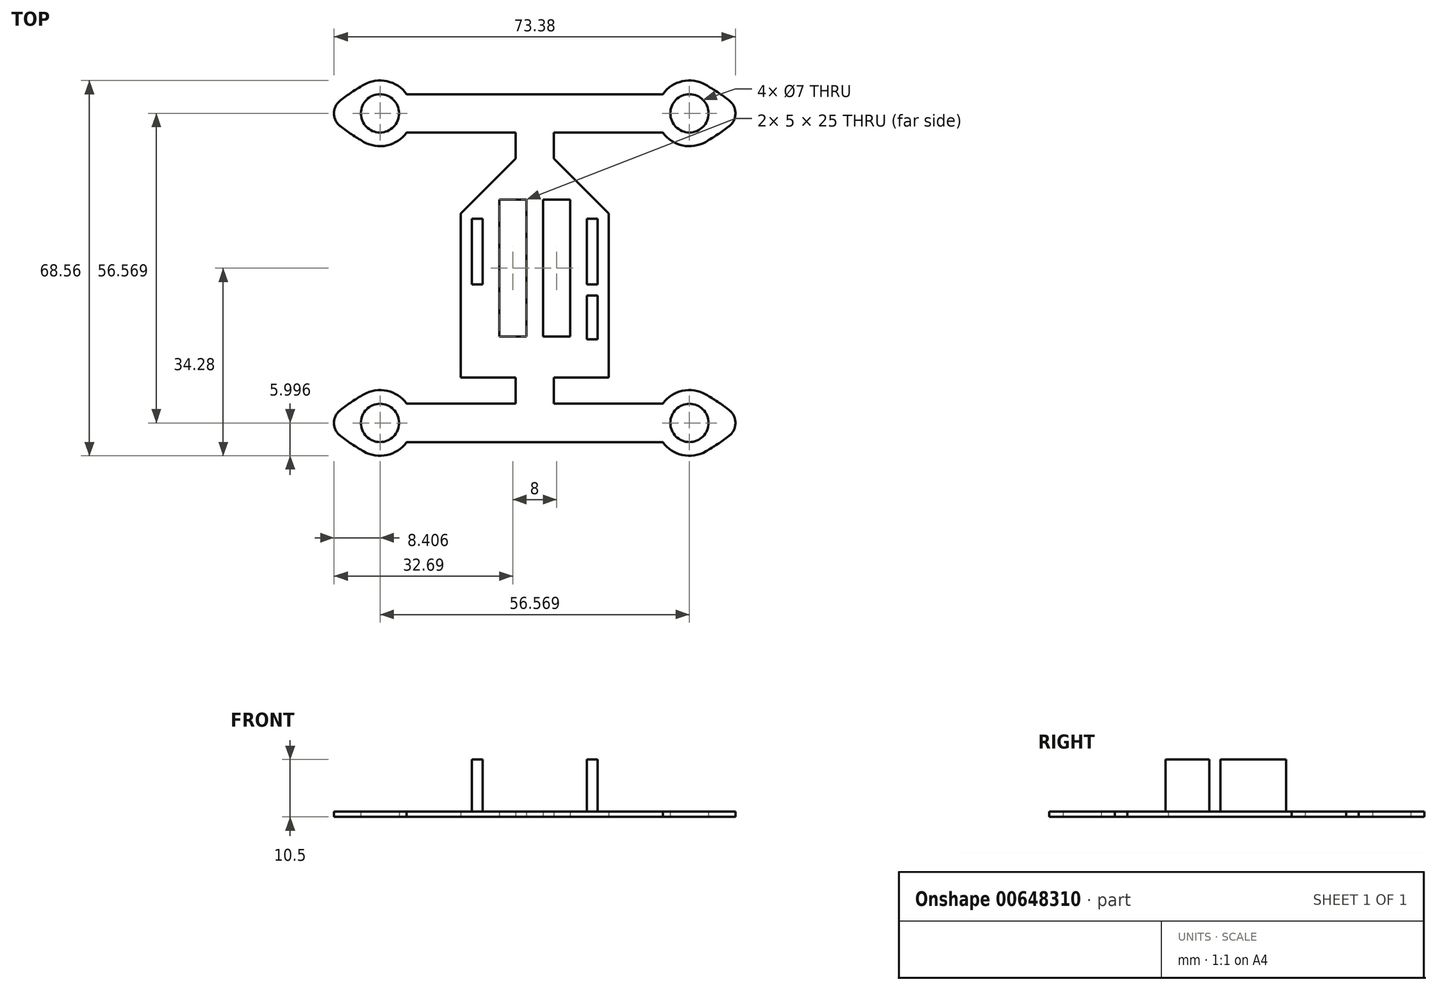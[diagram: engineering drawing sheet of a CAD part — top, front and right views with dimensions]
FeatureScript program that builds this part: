
annotation { "Feature Type Name" : "Feature", "Feature Type Description" : "" }
export const myFeature = defineFeature(function(context is Context, id is Id, definition is map)
    precondition{}
    {
        {
            var Q0;
            Q0=qCreatedBy(makeId("Top.planeOp"),FACE);
            var sketch = newSketch(context, id + "F0", { "sketchPlane" : qUnion([Q0])});
            skLineSegment(sketch, "E0.bottom", {"start": v(-28.28, 28.28) * mm, "end": v(28.28, 28.28) * mm, "construction": true});
            skLineSegment(sketch, "E0.top", {"start": v(-28.28, -28.28) * mm, "end": v(28.28, -28.28) * mm, "construction": true});
            skLineSegment(sketch, "E0.left", {"start": v(-28.28, 28.28) * mm, "end": v(-28.28, -28.28) * mm, "construction": true});
            skLineSegment(sketch, "E0.right", {"start": v(28.28, 28.28) * mm, "end": v(28.28, -28.28) * mm, "construction": true});
            skPoint(sketch, "E0.middle", {"position": v(0, 0) * mm});
            skLineSegment(sketch, "E1.top", {"start": v(-13.5, -20) * mm, "end": v(-3.5, -20) * mm});
            skLineSegment(sketch, "E1.left", {"start": v(-13.5, 10) * mm, "end": v(-13.5, -20) * mm});
            skLineSegment(sketch, "E1.right", {"start": v(13.5, 10) * mm, "end": v(13.5, -20) * mm});
            skArc(sketch, "E2", {"start": v(-31.28, 23.09) * mm, "mid": v(-27.02, 22.42) * mm, "end": v(-23.41, 24.78) * mm});
            skCircle(sketch, "E3", {"center": v(-28.28, 28.28) * mm, "radius": 3.5 * mm});
            skArc(sketch, "E4.MirrorC", {"start": v(31.28, 23.09) * mm, "mid": v(27.02, 22.42) * mm, "end": v(23.41, 24.78) * mm});
            skCircle(sketch, "E5.MirrorC", {"center": v(28.28, 28.28) * mm, "radius": 3.5 * mm});
            skArc(sketch, "E6.MirrorC", {"start": v(-23.41, -31.78) * mm, "mid": v(-27.02, -34.15) * mm, "end": v(-31.28, -33.48) * mm});
            skArc(sketch, "E7.MirrorC", {"start": v(23.41, -31.78) * mm, "mid": v(27.02, -34.15) * mm, "end": v(31.28, -33.48) * mm});
            skCircle(sketch, "E8.MirrorC", {"center": v(28.28, -28.28) * mm, "radius": 3.5 * mm});
            skCircle(sketch, "E9.MirrorC", {"center": v(-28.28, -28.28) * mm, "radius": 3.5 * mm});
            skLineSegment(sketch, "E10", {"start": v(-23.41, 31.78) * mm, "end": v(23.41, 31.78) * mm});
            skLineSegment(sketch, "E11.MirrorCS", {"start": v(-23.41, 24.78) * mm, "end": v(-3.5, 24.78) * mm});
            skLineSegment(sketch, "E12", {"start": v(-3.5, 24.78) * mm, "end": v(-3.5, 20) * mm});
            skPoint(sketch, "E12.endSnap0", {"position": v(0, 20) * mm});
            skLineSegment(sketch, "E13.MirrorCS", {"start": v(3.5, 24.78) * mm, "end": v(3.5, 20) * mm});
            skLineSegment(sketch, "E14.MirrorCS", {"start": v(23.41, 31.78) * mm, "end": v(-23.41, 31.78) * mm});
            skLineSegment(sketch, "E15.bottom", {"start": v(-1.5, 12.5) * mm, "end": v(-6.5, 12.5) * mm});
            skLineSegment(sketch, "E15.top", {"start": v(-1.5, -12.5) * mm, "end": v(-6.5, -12.5) * mm});
            skLineSegment(sketch, "E15.left", {"start": v(-1.5, 12.5) * mm, "end": v(-1.5, -12.5) * mm});
            skLineSegment(sketch, "E15.right", {"start": v(-6.5, 12.5) * mm, "end": v(-6.5, -12.5) * mm});
            skPoint(sketch, "E15.middle", {"position": v(-4, 0) * mm});
            skLineSegment(sketch, "E16", {"start": v(0, 40.4) * mm, "end": v(0, 0) * mm, "construction": true});
            skLineSegment(sketch, "E17", {"start": v(0, 0) * mm, "end": v(38.65, 0) * mm, "construction": true});
            skLineSegment(sketch, "E18.MirrorCS", {"start": v(1.5, 12.5) * mm, "end": v(1.5, -12.5) * mm});
            skPoint(sketch, "E19.MirrorP", {"position": v(4, 0) * mm});
            skLineSegment(sketch, "E20.MirrorCS", {"start": v(6.5, 12.5) * mm, "end": v(6.5, -12.5) * mm});
            skLineSegment(sketch, "E21.MirrorCS", {"start": v(1.5, 12.5) * mm, "end": v(6.5, 12.5) * mm});
            skLineSegment(sketch, "E22.MirrorCS", {"start": v(1.5, -12.5) * mm, "end": v(6.5, -12.5) * mm});
            skArc(sketch, "E23.MirrorC", {"start": v(-23.41, 31.78) * mm, "mid": v(-27.02, 34.15) * mm, "end": v(-31.28, 33.48) * mm});
            skArc(sketch, "E24", {"start": v(35.5, 30.67) * mm, "mid": v(33.44, 32.14) * mm, "end": v(31.28, 33.48) * mm});
            skArc(sketch, "E25", {"start": v(31.28, 23.09) * mm, "mid": v(33.44, 24.43) * mm, "end": v(35.5, 25.9) * mm});
            skArc(sketch, "E26.filletArc", {"start": v(35.5, 25.9) * mm, "mid": v(36.69, 28.28) * mm, "end": v(35.5, 30.67) * mm});
            skArc(sketch, "E27.MirrorCS", {"start": v(-31.28, 23.09) * mm, "mid": v(-33.44, 24.43) * mm, "end": v(-35.5, 25.9) * mm});
            skArc(sketch, "E28.MirrorCS", {"start": v(-35.5, 25.9) * mm, "mid": v(-36.69, 28.28) * mm, "end": v(-35.5, 30.67) * mm});
            skArc(sketch, "E29.MirrorCS", {"start": v(-35.5, 30.67) * mm, "mid": v(-33.44, 32.14) * mm, "end": v(-31.28, 33.48) * mm});
            skArc(sketch, "E30.MirrorCS", {"start": v(-35.5, -30.67) * mm, "mid": v(-33.44, -32.14) * mm, "end": v(-31.28, -33.48) * mm});
            skArc(sketch, "E31.MirrorC", {"start": v(-31.28, -23.09) * mm, "mid": v(-27.02, -22.42) * mm, "end": v(-23.41, -24.78) * mm});
            skLineSegment(sketch, "E32.MirrorCS", {"start": v(23.41, -31.78) * mm, "end": v(-23.41, -31.78) * mm});
            skLineSegment(sketch, "E33.MirrorCS", {"start": v(-3.5, -24.78) * mm, "end": v(-3.5, -20) * mm});
            skArc(sketch, "E34.MirrorCS", {"start": v(31.28, -23.09) * mm, "mid": v(33.44, -24.43) * mm, "end": v(35.5, -25.9) * mm});
            skLineSegment(sketch, "E35.MirrorCS", {"start": v(-23.41, -24.78) * mm, "end": v(-3.5, -24.78) * mm});
            skArc(sketch, "E36.MirrorCS", {"start": v(-35.5, -25.9) * mm, "mid": v(-36.69, -28.28) * mm, "end": v(-35.5, -30.67) * mm});
            skPoint(sketch, "E37.MirrorP", {"position": v(0, -20) * mm});
            skLineSegment(sketch, "E38.MirrorCS", {"start": v(3.5, -24.78) * mm, "end": v(3.5, -20) * mm});
            skArc(sketch, "E39.MirrorCS", {"start": v(35.5, -25.9) * mm, "mid": v(36.69, -28.28) * mm, "end": v(35.5, -30.67) * mm});
            skArc(sketch, "E40.MirrorCS", {"start": v(-31.28, -23.09) * mm, "mid": v(-33.44, -24.43) * mm, "end": v(-35.5, -25.9) * mm});
            skArc(sketch, "E41.MirrorC", {"start": v(31.28, -23.09) * mm, "mid": v(29.84, -22.49) * mm, "end": v(28.28, -22.28) * mm});
            skLineSegment(sketch, "E42.MirrorCS", {"start": v(-23.41, -31.78) * mm, "end": v(23.41, -31.78) * mm});
            skArc(sketch, "E43.MirrorCS", {"start": v(35.5, -30.67) * mm, "mid": v(33.44, -32.14) * mm, "end": v(31.28, -33.48) * mm});
            skLineSegment(sketch, "E44.MirrorCS", {"start": v(13.5, -20) * mm, "end": v(13.5, 10) * mm});
            skLineSegment(sketch, "E45", {"start": v(3.5, 20) * mm, "end": v(13.5, 10) * mm});
            skLineSegment(sketch, "E46.trimOffspring", {"start": v(3.5, 24.78) * mm, "end": v(23.41, 24.78) * mm});
            skLineSegment(sketch, "E47.trimOffspring", {"start": v(3.5, 20) * mm, "end": v(13.5, 20) * mm, "construction": true});
            skArc(sketch, "E48.trimOffspring", {"start": v(23.41, 31.78) * mm, "mid": v(27.02, 34.15) * mm, "end": v(31.28, 33.48) * mm});
            skPoint(sketch, "E49.orphan", {"position": v(13.5, 20) * mm});
            skLineSegment(sketch, "E50.trimOffspring", {"start": v(3.5, -20) * mm, "end": v(13.5, -20) * mm});
            skLineSegment(sketch, "E51.trimOffspring", {"start": v(3.5, -24.78) * mm, "end": v(23.41, -24.78) * mm});
            skArc(sketch, "E52.trimOffspring", {"start": v(31.28, -23.09) * mm, "mid": v(27.02, -22.42) * mm, "end": v(23.41, -24.78) * mm});
            skLineSegment(sketch, "E53.MirrorCS", {"start": v(-3.5, 20) * mm, "end": v(-13.5, 10) * mm});
            skPoint(sketch, "E54.MirrorCS.end.orphan", {"position": v(-13.5, 20) * mm});
            skPoint(sketch, "E54.MirrorCS.start.orphan", {"position": v(-3.5, 20) * mm});
            skPoint(sketch, "E1.bottom.start.orphan", {"position": v(-13.5, 20) * mm});
            skLineSegment(sketch, "E55.left", {"start": v(-11.56, 9) * mm, "end": v(-11.56, 9) * mm});
            skLineSegment(sketch, "E55.right", {"start": v(-9.56, 9) * mm, "end": v(-9.56, 9) * mm});
            skSolve(sketch);
        }
        {
            var Q0;
            Q0 = qSketchRegion(id + "F0", true);
            extrude(context, id + "F1", {"entities" : qUnion([Q0]), "depth" : 1 * mm, "offsetDistance" : 25 * mm});
        }
        {
            var Q0;
            Q0=makeQuery(id+"F1.opExtrude","CAP_FACE",FACE,{"disambiguationData":[OSD([sQuery(id+"F0.wireOp",EDGE,"E1.left"),sQuery(id+"F0.wireOp",EDGE,"E4.MirrorC"),sQuery(id+"F0.wireOp",EDGE,"E5.MirrorC"),sQuery(id+"F0.wireOp",EDGE,"E11.MirrorCS"),sQuery(id+"F0.wireOp",EDGE,"E12"),sQuery(id+"F0.wireOp",EDGE,"E13.MirrorCS"),sQuery(id+"F0.wireOp",EDGE,"E14.MirrorCS"),sQuery(id+"F0.wireOp",EDGE,"E15.top"),sQuery(id+"F0.wireOp",EDGE,"E15.left"),sQuery(id+"F0.wireOp",EDGE,"E15.right"),sQuery(id+"F0.wireOp",EDGE,"E18.MirrorCS"),sQuery(id+"F0.wireOp",EDGE,"E20.MirrorCS"),sQuery(id+"F0.wireOp",EDGE,"E21.MirrorCS"),sQuery(id+"F0.wireOp",EDGE,"E22.MirrorCS"),sQuery(id+"F0.wireOp",EDGE,"E24"),sQuery(id+"F0.wireOp",EDGE,"E25"),sQuery(id+"F0.wireOp",EDGE,"E26.filletArc"),sQuery(id+"F0.wireOp",EDGE,"E27.MirrorCS"),sQuery(id+"F0.wireOp",EDGE,"E28.MirrorCS"),sQuery(id+"F0.wireOp",EDGE,"E3"),sQuery(id+"F0.wireOp",EDGE,"E29.MirrorCS"),sQuery(id+"F0.wireOp",EDGE,"E30.MirrorCS"),sQuery(id+"F0.wireOp",EDGE,"E33.MirrorCS"),sQuery(id+"F0.wireOp",EDGE,"E34.MirrorCS"),sQuery(id+"F0.wireOp",EDGE,"E35.MirrorCS"),sQuery(id+"F0.wireOp",EDGE,"E6.MirrorC"),sQuery(id+"F0.wireOp",EDGE,"E36.MirrorCS"),sQuery(id+"F0.wireOp",EDGE,"E1.top"),sQuery(id+"F0.wireOp",EDGE,"E38.MirrorCS"),sQuery(id+"F0.wireOp",EDGE,"E39.MirrorCS"),sQuery(id+"F0.wireOp",EDGE,"E40.MirrorCS"),sQuery(id+"F0.wireOp",EDGE,"E9.MirrorC"),sQuery(id+"F0.wireOp",EDGE,"E42.MirrorCS"),sQuery(id+"F0.wireOp",EDGE,"E43.MirrorCS"),sQuery(id+"F0.wireOp",EDGE,"E8.MirrorC"),sQuery(id+"F0.wireOp",EDGE,"E7.MirrorC"),sQuery(id+"F0.wireOp",EDGE,"E44.MirrorCS"),sQuery(id+"F0.wireOp",EDGE,"E45"),sQuery(id+"F0.wireOp",EDGE,"E46.trimOffspring"),sQuery(id+"F0.wireOp",EDGE,"E48.trimOffspring"),sQuery(id+"F0.wireOp",EDGE,"E2"),sQuery(id+"F0.wireOp",EDGE,"E23.MirrorC"),sQuery(id+"F0.wireOp",EDGE,"E31.MirrorC"),sQuery(id+"F0.wireOp",EDGE,"E50.trimOffspring"),sQuery(id+"F0.wireOp",EDGE,"E51.trimOffspring"),sQuery(id+"F0.wireOp",EDGE,"E52.trimOffspring"),sQuery(id+"F0.wireOp",EDGE,"E15.bottom"),sQuery(id+"F0.wireOp",EDGE,"E53.MirrorCS")])],"isStart":false});
            var sketch = newSketch(context, id + "F2", { "sketchPlane" : qUnion([Q0])});
            skLineSegment(sketch, "E56.bottom", {"start": v(-11.5, 9) * mm, "end": v(-9.5, 9) * mm});
            skLineSegment(sketch, "E56.top", {"start": v(-11.5, -3) * mm, "end": v(-9.5, -3) * mm});
            skLineSegment(sketch, "E56.left", {"start": v(-11.5, 9) * mm, "end": v(-11.5, -3) * mm});
            skLineSegment(sketch, "E56.right", {"start": v(-9.5, 9) * mm, "end": v(-9.5, -3) * mm});
            skLineSegment(sketch, "E57.bottom", {"start": v(9.5, 9) * mm, "end": v(11.5, 9) * mm});
            skLineSegment(sketch, "E57.top", {"start": v(9.5, -3) * mm, "end": v(11.5, -3) * mm});
            skLineSegment(sketch, "E57.left", {"start": v(9.5, 9) * mm, "end": v(9.5, -3) * mm});
            skLineSegment(sketch, "E57.right", {"start": v(11.5, 9) * mm, "end": v(11.5, -3) * mm});
            skPoint(sketch, "E58.firstSnap0", {"position": v(13.5, -5) * mm});
            skPoint(sketch, "E58.bottom.end.orphan", {"position": v(10.15, -5) * mm});
            skPoint(sketch, "E58.left.start.orphan", {"position": v(8.15, -5) * mm});
            skLineSegment(sketch, "E59.bottom", {"start": v(9.5, -5) * mm, "end": v(11.5, -5) * mm});
            skLineSegment(sketch, "E59.top", {"start": v(9.5, -13) * mm, "end": v(11.5, -13) * mm});
            skLineSegment(sketch, "E59.left", {"start": v(9.5, -5) * mm, "end": v(9.5, -13) * mm});
            skLineSegment(sketch, "E59.right", {"start": v(11.5, -5) * mm, "end": v(11.5, -13) * mm});
            skSolve(sketch);
        }
        {
            var Q0;
            Q0 = qSketchRegion(id + "F2", true);
            extrude(context, id + "F3", {"entities" : qUnion([Q0]), "operationType" : NewBodyOperationType.ADD, "depth" : 9.5 * mm, "offsetDistance" : 25 * mm});
        }
    });
